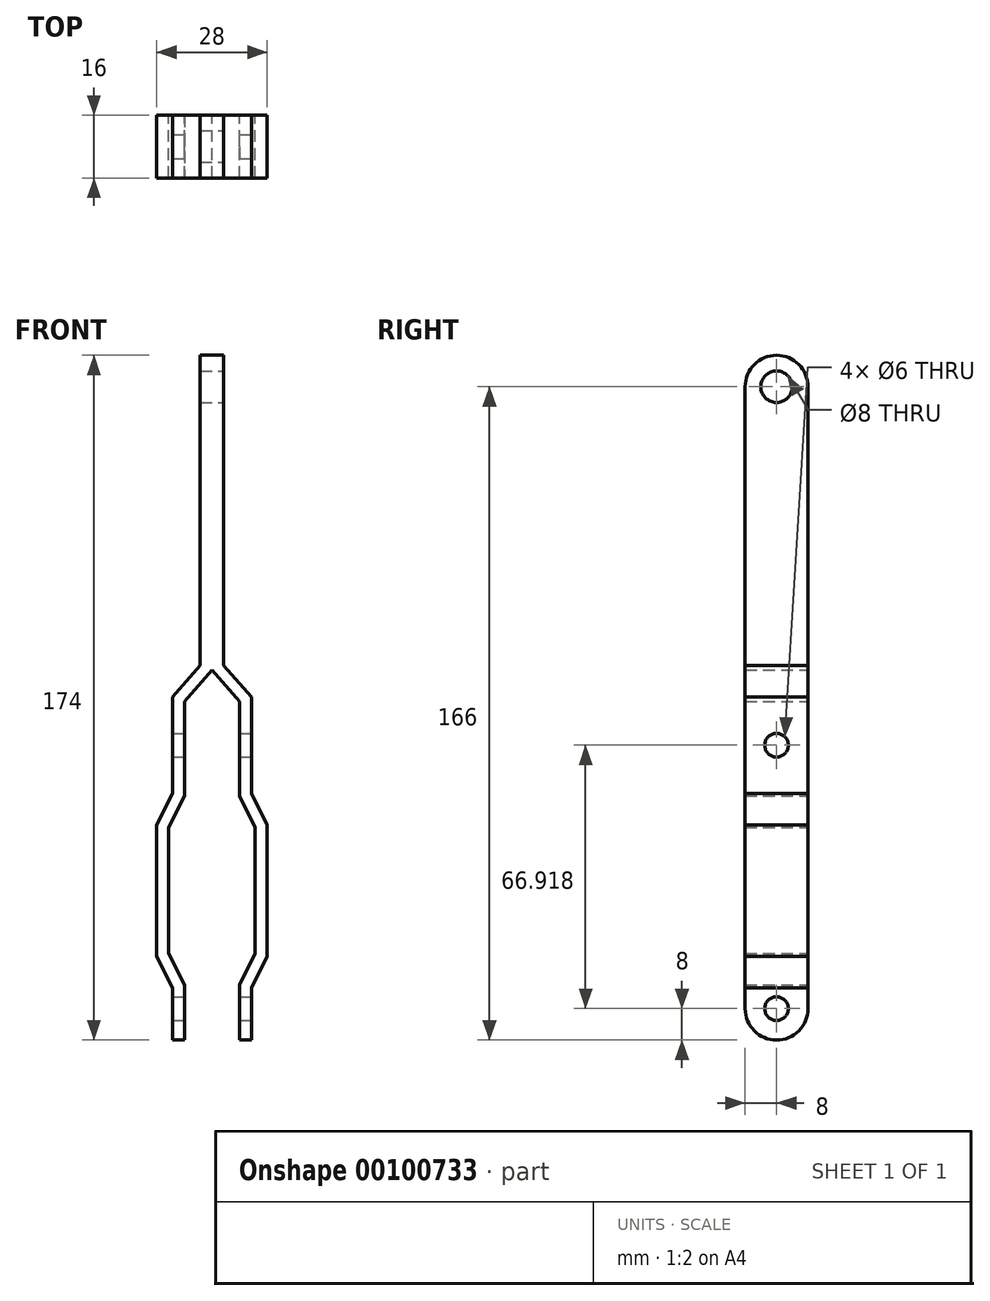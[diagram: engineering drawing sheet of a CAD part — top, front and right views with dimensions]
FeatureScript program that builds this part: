
annotation { "Feature Type Name" : "Feature", "Feature Type Description" : "" }
export const myFeature = defineFeature(function(context is Context, id is Id, definition is map)
    precondition{}
    {
        {
            var Q0;
            Q0=qCreatedBy(makeId("Front.planeOp"),FACE);
            var sketch = newSketch(context, id + "F0", { "sketchPlane" : qUnion([Q0])});
            skLineSegment(sketch, "E0", {"start": v(0, 72) * mm, "end": v(0, 0) * mm});
            skLineSegment(sketch, "E1", {"start": v(0, 0) * mm, "end": v(-7, -8) * mm});
            skLineSegment(sketch, "E2", {"start": v(-7, -8) * mm, "end": v(-7, -32) * mm});
            skLineSegment(sketch, "E3", {"start": v(-7, -32) * mm, "end": v(-11, -40) * mm});
            skLineSegment(sketch, "E4", {"start": v(-11, -40) * mm, "end": v(-11, -72) * mm});
            skLineSegment(sketch, "E5", {"start": v(-11, -72) * mm, "end": v(-7, -80) * mm});
            skLineSegment(sketch, "E6", {"start": v(-7, -80) * mm, "end": v(-7, -86) * mm});
            skLineSegment(sketch, "E7", {"start": v(0, 0) * mm, "end": v(0, -81.67) * mm, "construction": true});
            skLineSegment(sketch, "E8.0", {"start": v(-10, -80.7) * mm, "end": v(-10, -86) * mm});
            skLineSegment(sketch, "E8.1", {"start": v(-14, -72.7) * mm, "end": v(-10, -80.7) * mm});
            skLineSegment(sketch, "E8.2", {"start": v(-14, -39.3) * mm, "end": v(-14, -72.7) * mm});
            skLineSegment(sketch, "E8.3", {"start": v(-3, 72) * mm, "end": v(-3, 1.13) * mm});
            skLineSegment(sketch, "E8.4", {"start": v(-3, 1.13) * mm, "end": v(-10, -6.87) * mm});
            skLineSegment(sketch, "E8.5", {"start": v(-10, -6.87) * mm, "end": v(-10, -31.3) * mm});
            skLineSegment(sketch, "E8.6", {"start": v(-10, -31.3) * mm, "end": v(-14, -39.3) * mm});
            skLineSegment(sketch, "E9", {"start": v(0, 72) * mm, "end": v(-3, 72) * mm});
            skLineSegment(sketch, "E10", {"start": v(-7, -86) * mm, "end": v(-10, -86) * mm});
            skSolve(sketch);
        }
        {
            var Q0;
            Q0 = qSketchRegion(id + "F0", true);
            extrude(context, id + "F1", {"entities" : qUnion([Q0]), "depth" : 16 * mm});
        }
        {
            var Q0;
            Q0=makeQuery(id+"F1.opExtrude","SWEPT_BODY",BODY,{"disambiguationData":[OSD([sQuery(id+"F0.wireOp",EDGE,"E0"),sQuery(id+"F0.wireOp",EDGE,"E1"),sQuery(id+"F0.wireOp",EDGE,"E2"),sQuery(id+"F0.wireOp",EDGE,"E3"),sQuery(id+"F0.wireOp",EDGE,"E4"),sQuery(id+"F0.wireOp",EDGE,"E5"),sQuery(id+"F0.wireOp",EDGE,"E6"),sQuery(id+"F0.wireOp",EDGE,"E8.0"),sQuery(id+"F0.wireOp",EDGE,"E8.1"),sQuery(id+"F0.wireOp",EDGE,"E8.2"),sQuery(id+"F0.wireOp",EDGE,"E8.3"),sQuery(id+"F0.wireOp",EDGE,"E8.4"),sQuery(id+"F0.wireOp",EDGE,"E8.5"),sQuery(id+"F0.wireOp",EDGE,"E8.6"),sQuery(id+"F0.wireOp",EDGE,"E9"),sQuery(id+"F0.wireOp",EDGE,"E10")])]});
            var Q1;
            Q1=qCreatedBy(makeId("Right.planeOp"),FACE);
            mirror(context, id + "F2", {"operationType" : NewBodyOperationType.ADD, "entities" : qUnion([Q0]), "mirrorPlane" : qUnion([Q1])});
        }
        {
            var Q0;
            Q0=makeQuery(id+"F2.opPattern","COPY",FACE,{"derivedFrom":makeQuery(id+"F1.opExtrude","SWEPT_FACE",FACE,{"disambiguationData":[OSD([sQuery(id+"F0.wireOp",EDGE,"E8.3")])]}),"instanceName":"1"});
            var sketch = newSketch(context, id + "F3", { "sketchPlane" : qUnion([Q0])});
            skArc(sketch, "E11", {"start": v(0, 72) * mm, "mid": v(-8, 80) * mm, "end": v(-16, 72) * mm});
            skSolve(sketch);
        }
        {
            var Q0;
            Q0=makeQuery(id+"F2.opPattern","COPY",FACE,{"derivedFrom":makeQuery(id+"F1.opExtrude","SWEPT_FACE",FACE,{"disambiguationData":[OSD([sQuery(id+"F0.wireOp",EDGE,"E8.0")])]}),"instanceName":"1"});
            var sketch = newSketch(context, id + "F4", { "sketchPlane" : qUnion([Q0])});
            skArc(sketch, "E12", {"start": v(-16, -86) * mm, "mid": v(-8, -94) * mm, "end": v(0, -86) * mm});
            skSolve(sketch);
        }
        {
            var Q0;
            Q0=makeQuery(id+"F1.opExtrude","SWEPT_FACE",FACE,{"disambiguationData":[OSD([sQuery(id+"F0.wireOp",EDGE,"E8.0")])]});
            var sketch = newSketch(context, id + "F5", { "sketchPlane" : qUnion([Q0])});
            skArc(sketch, "E13", {"start": v(0, -86) * mm, "mid": v(8, -94) * mm, "end": v(16, -86) * mm});
            skSolve(sketch);
        }
        {
            var Q0;
            Q0=makeQuery(id+"F3.imprint","IMPRINT",FACE,{"disambiguationData":[TD([[makeQuery(id+"F3.imprint","IMPRINT",EDGE,{"derivedFrom":sQuery(id+"F3.wireOp",EDGE,"E11")}),1.0]])]});
            extrude(context, id + "F6", {"entities" : qUnion([Q0]), "operationType" : NewBodyOperationType.ADD, "oppositeDirection" : true, "depth" : 6 * mm});
        }
        {
            var Q0;
            Q0=makeQuery(id+"F5.imprint","IMPRINT",FACE,{"disambiguationData":[TD([[makeQuery(id+"F5.imprint","IMPRINT",EDGE,{"derivedFrom":sQuery(id+"F5.wireOp",EDGE,"E13")}),1.0]])]});
            extrude(context, id + "F7", {"entities" : qUnion([Q0]), "operationType" : NewBodyOperationType.ADD, "oppositeDirection" : true, "depth" : 3 * mm});
        }
        {
            var Q0;
            Q0=makeQuery(id+"F4.imprint","IMPRINT",FACE,{"disambiguationData":[TD([[makeQuery(id+"F4.imprint","IMPRINT",EDGE,{"derivedFrom":sQuery(id+"F4.wireOp",EDGE,"E12")}),1.0]])]});
            extrude(context, id + "F8", {"entities" : qUnion([Q0]), "operationType" : NewBodyOperationType.ADD, "oppositeDirection" : true, "depth" : 3 * mm});
        }
        {
            var Q0;
            {var subQ0=sQuery(id+"F0.wireOp",EDGE,"E8.3");Q0=makeQuery(id+"F6.boolean.opBoolean","MERGE",FACE,{"derivedFrom":[makeQuery(id+"F2.opPattern","COPY",FACE,{"derivedFrom":makeQuery(id+"F1.opExtrude","SWEPT_FACE",FACE,{"disambiguationData":[OSD([subQ0])]}),"instanceName":"1"}),makeQuery(id+"F6.opExtrude","CAP_FACE",FACE,{"disambiguationData":[OSD([subQ0,sQuery(id+"F0.wireOp",EDGE,"E9"),sQuery(id+"F3.wireOp",EDGE,"E11")])],"isStart":true})]});}
            var sketch = newSketch(context, id + "F9", { "sketchPlane" : qUnion([Q0])});
            skCircle(sketch, "E14", {"center": v(-8, 72) * mm, "radius": 4 * mm});
            skSolve(sketch);
        }
        {
            var Q0;
            {var subQ0=sQuery(id+"F0.wireOp",EDGE,"E8.0");Q0=makeQuery(id+"F8.boolean.opBoolean","MERGE",FACE,{"derivedFrom":[makeQuery(id+"F2.opPattern","COPY",FACE,{"derivedFrom":makeQuery(id+"F1.opExtrude","SWEPT_FACE",FACE,{"disambiguationData":[OSD([subQ0])]}),"instanceName":"1"}),makeQuery(id+"F8.opExtrude","CAP_FACE",FACE,{"disambiguationData":[OSD([subQ0,sQuery(id+"F0.wireOp",EDGE,"E10"),sQuery(id+"F4.wireOp",EDGE,"E12")])],"isStart":true})]});}
            var sketch = newSketch(context, id + "F10", { "sketchPlane" : qUnion([Q0])});
            skCircle(sketch, "E15", {"center": v(-8, -86) * mm, "radius": 3 * mm});
            skSolve(sketch);
        }
        {
            var Q0;
            Q0=makeQuery(id+"F2.opPattern","COPY",FACE,{"derivedFrom":makeQuery(id+"F1.opExtrude","SWEPT_FACE",FACE,{"disambiguationData":[OSD([sQuery(id+"F0.wireOp",EDGE,"E8.5")])]}),"instanceName":"1"});
            var sketch = newSketch(context, id + "F11", { "sketchPlane" : qUnion([Q0])});
            skCircle(sketch, "E16", {"center": v(-8, -19.08) * mm, "radius": 3 * mm});
            skPoint(sketch, "E16.centerSnap0", {"position": v(0, -19.08) * mm});
            skLineSegment(sketch, "E17", {"start": v(-8, -6.87) * mm, "end": v(-8, -31.3) * mm, "construction": true});
            skSolve(sketch);
        }
        {
            var Q0;
            Q0=makeQuery(id+"F9.imprint","IMPRINT",FACE,{"disambiguationData":[TD([[makeQuery(id+"F9.imprint","IMPRINT",EDGE,{"derivedFrom":sQuery(id+"F9.wireOp",EDGE,"E14")}),1.0]])]});
            extrude(context, id + "F12", {"entities" : qUnion([Q0]), "operationType" : NewBodyOperationType.REMOVE, "oppositeDirection" : true, "depth" : 25 * mm});
        }
        {
            var Q0;
            Q0=makeQuery(id+"F11.imprint","IMPRINT",FACE,{"disambiguationData":[TD([[makeQuery(id+"F11.imprint","IMPRINT",EDGE,{"derivedFrom":sQuery(id+"F11.wireOp",EDGE,"E16")}),1.0]])]});
            extrude(context, id + "F13", {"entities" : qUnion([Q0]), "operationType" : NewBodyOperationType.REMOVE, "oppositeDirection" : true, "depth" : 50 * mm});
        }
        {
            var Q0;
            Q0=makeQuery(id+"F10.imprint","IMPRINT",FACE,{"disambiguationData":[TD([[makeQuery(id+"F10.imprint","IMPRINT",EDGE,{"derivedFrom":sQuery(id+"F10.wireOp",EDGE,"E15")}),1.0]])]});
            extrude(context, id + "F14", {"entities" : qUnion([Q0]), "operationType" : NewBodyOperationType.REMOVE, "oppositeDirection" : true, "depth" : 50 * mm});
        }
    });
